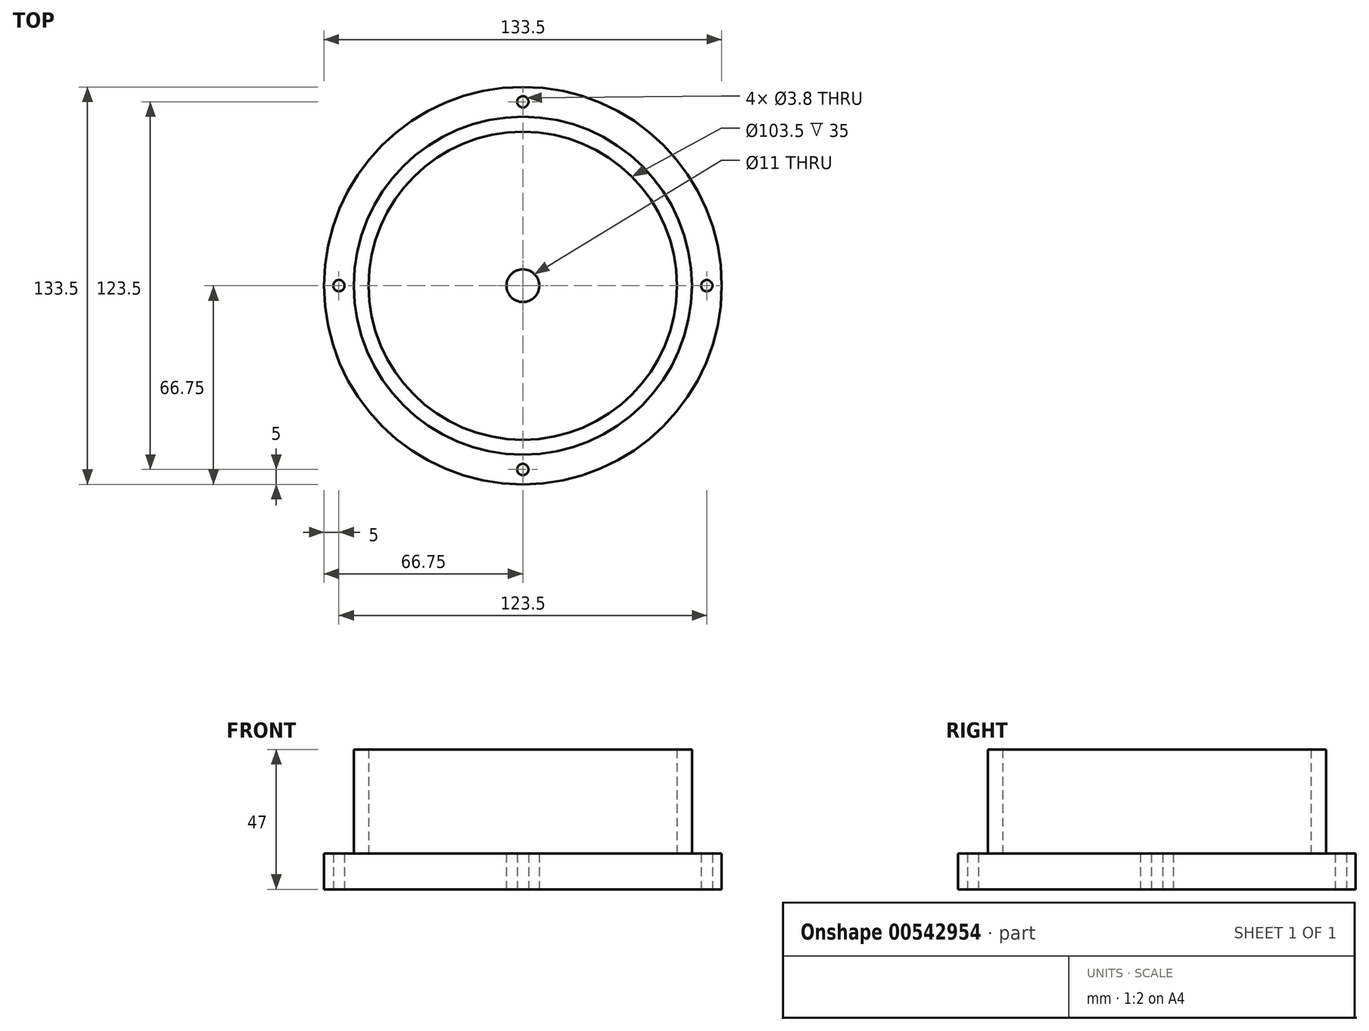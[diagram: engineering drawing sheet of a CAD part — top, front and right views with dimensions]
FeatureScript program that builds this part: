
annotation { "Feature Type Name" : "Feature", "Feature Type Description" : "" }
export const myFeature = defineFeature(function(context is Context, id is Id, definition is map)
    precondition{}
    {
        {
            var Q0;
            Q0=qCreatedBy(makeId("Top.planeOp"),FACE);
            var sketch = newSketch(context, id + "F0", { "sketchPlane" : qUnion([Q0])});
            skCircle(sketch, "E0", {"center": v(0, 0) * mm, "radius": 66.75 * mm});
            skSolve(sketch);
        }
        {
            var Q0;
            Q0 = qSketchRegion(id + "F0", true);
            extrude(context, id + "F1", {"entities" : qUnion([Q0]), "depth" : 12 * mm, "offsetDistance" : 25 * mm});
        }
        {
            var Q0;
            Q0=makeQuery(id+"F1.opExtrude","CAP_FACE",FACE,{"disambiguationData":[OSD([sQuery(id+"F0.wireOp",EDGE,"E0")])],"isStart":false});
            var sketch = newSketch(context, id + "F2", { "sketchPlane" : qUnion([Q0])});
            skCircle(sketch, "E1", {"center": v(0, 0) * mm, "radius": 56.75 * mm});
            skCircle(sketch, "E2", {"center": v(0, 0) * mm, "radius": 51.75 * mm});
            skSolve(sketch);
        }
        {
            var Q0;
            Q0=makeQuery(id+"F2.imprint","IMPRINT",FACE,{"disambiguationData":[TD([[makeQuery(id+"F2.imprint","IMPRINT",EDGE,{"derivedFrom":sQuery(id+"F2.wireOp",EDGE,"E1")}),1.0]])]});
            extrude(context, id + "F3", {"entities" : qUnion([Q0]), "operationType" : NewBodyOperationType.ADD, "depth" : 35 * mm, "offsetDistance" : 25 * mm});
        }
        {
            var Q0;
            Q0=qCreatedBy(makeId("Top.planeOp"),FACE);
            var sketch = newSketch(context, id + "F4", { "sketchPlane" : qUnion([Q0])});
            skCircle(sketch, "E3", {"center": v(0, 0) * mm, "radius": 61.75 * mm, "construction": true});
            skSolve(sketch);
        }
        {
            var Q0;
            Q0=qCreatedBy(makeId("Top.planeOp"),FACE);
            var sketch = newSketch(context, id + "F5", { "sketchPlane" : qUnion([Q0])});
            skCircle(sketch, "E4.0", {"center": v(0, 0) * mm, "radius": 61.75 * mm});
            skCircle(sketch, "E5", {"center": v(-61.75, 0) * mm, "radius": 1.9 * mm});
            skCircle(sketch, "E6", {"center": v(0, -61.75) * mm, "radius": 1.9 * mm});
            skCircle(sketch, "E7", {"center": v(61.75, 0) * mm, "radius": 1.9 * mm});
            skCircle(sketch, "E8", {"center": v(0, 61.75) * mm, "radius": 1.9 * mm});
            skSolve(sketch);
        }
        {
            var Q0;
            {var subQ0=sQuery(id+"F5.wireOp",EDGE,"E8");var subQ1=sQuery(id+"F5.wireOp",EDGE,"E4.0");var subQ2=makeQuery(id+"F5.imprint","INTERSECT",VERTEX,{"disambiguationData":[OD(0.0)],"derivedFrom":[subQ1,subQ0]});Q0=makeQuery(id+"F5.imprint","IMPRINT",FACE,{"disambiguationData":[TD([[makeQuery(id+"F5.imprint","IMPRINT",EDGE,{"disambiguationData":[TD([[subQ2,-1.0]])],"derivedFrom":subQ1}),1.0]])]});}
            var Q1;
            {var subQ0=sQuery(id+"F5.wireOp",EDGE,"E8");var subQ1=sQuery(id+"F5.wireOp",EDGE,"E4.0");var subQ2=makeQuery(id+"F5.imprint","INTERSECT",VERTEX,{"disambiguationData":[OD(0.0)],"derivedFrom":[subQ1,subQ0]});Q1=makeQuery(id+"F5.imprint","IMPRINT",FACE,{"disambiguationData":[TD([[makeQuery(id+"F5.imprint","IMPRINT",EDGE,{"disambiguationData":[TD([[subQ2,-1.0]])],"derivedFrom":subQ1}),-1.0]])]});}
            var Q2;
            {var subQ0=sQuery(id+"F5.wireOp",EDGE,"E7");var subQ1=sQuery(id+"F5.wireOp",EDGE,"E4.0");var subQ2=makeQuery(id+"F5.imprint","INTERSECT",VERTEX,{"disambiguationData":[OD(0.0)],"derivedFrom":[subQ1,subQ0]});Q2=makeQuery(id+"F5.imprint","IMPRINT",FACE,{"disambiguationData":[TD([[makeQuery(id+"F5.imprint","IMPRINT",EDGE,{"disambiguationData":[TD([[subQ2,1.0]])],"derivedFrom":subQ1}),-1.0]])]});}
            var Q3;
            {var subQ0=sQuery(id+"F5.wireOp",EDGE,"E7");var subQ1=sQuery(id+"F5.wireOp",EDGE,"E4.0");var subQ2=makeQuery(id+"F5.imprint","INTERSECT",VERTEX,{"disambiguationData":[OD(0.0)],"derivedFrom":[subQ1,subQ0]});Q3=makeQuery(id+"F5.imprint","IMPRINT",FACE,{"disambiguationData":[TD([[makeQuery(id+"F5.imprint","IMPRINT",EDGE,{"disambiguationData":[TD([[subQ2,1.0]])],"derivedFrom":subQ1}),1.0]])]});}
            var Q4;
            {var subQ0=sQuery(id+"F5.wireOp",EDGE,"E6");var subQ1=sQuery(id+"F5.wireOp",EDGE,"E4.0");var subQ2=makeQuery(id+"F5.imprint","INTERSECT",VERTEX,{"disambiguationData":[OD(0.0)],"derivedFrom":[subQ1,subQ0]});Q4=makeQuery(id+"F5.imprint","IMPRINT",FACE,{"disambiguationData":[TD([[makeQuery(id+"F5.imprint","IMPRINT",EDGE,{"disambiguationData":[TD([[subQ2,-1.0]])],"derivedFrom":subQ1}),-1.0]])]});}
            var Q5;
            {var subQ0=sQuery(id+"F5.wireOp",EDGE,"E6");var subQ1=sQuery(id+"F5.wireOp",EDGE,"E4.0");var subQ2=makeQuery(id+"F5.imprint","INTERSECT",VERTEX,{"disambiguationData":[OD(0.0)],"derivedFrom":[subQ1,subQ0]});Q5=makeQuery(id+"F5.imprint","IMPRINT",FACE,{"disambiguationData":[TD([[makeQuery(id+"F5.imprint","IMPRINT",EDGE,{"disambiguationData":[TD([[subQ2,-1.0]])],"derivedFrom":subQ1}),1.0]])]});}
            var Q6;
            {var subQ0=sQuery(id+"F5.wireOp",EDGE,"E5");var subQ1=sQuery(id+"F5.wireOp",EDGE,"E4.0");var subQ2=makeQuery(id+"F5.imprint","INTERSECT",VERTEX,{"disambiguationData":[OD(0.0)],"derivedFrom":[subQ1,subQ0]});Q6=makeQuery(id+"F5.imprint","IMPRINT",FACE,{"disambiguationData":[TD([[makeQuery(id+"F5.imprint","IMPRINT",EDGE,{"disambiguationData":[TD([[subQ2,-1.0]])],"derivedFrom":subQ1}),1.0]])]});}
            var Q7;
            {var subQ0=sQuery(id+"F5.wireOp",EDGE,"E5");var subQ1=sQuery(id+"F5.wireOp",EDGE,"E4.0");var subQ2=makeQuery(id+"F5.imprint","INTERSECT",VERTEX,{"disambiguationData":[OD(0.0)],"derivedFrom":[subQ1,subQ0]});Q7=makeQuery(id+"F5.imprint","IMPRINT",FACE,{"disambiguationData":[TD([[makeQuery(id+"F5.imprint","IMPRINT",EDGE,{"disambiguationData":[TD([[subQ2,-1.0]])],"derivedFrom":subQ1}),-1.0]])]});}
            extrude(context, id + "F6", {"entities" : qUnion([Q0, Q1, Q2, Q3, Q4, Q5, Q6, Q7]), "operationType" : NewBodyOperationType.REMOVE, "depth" : 12 * mm, "offsetDistance" : 25 * mm});
        }
        {
            var Q0;
            Q0=qCreatedBy(makeId("Top.planeOp"),FACE);
            var sketch = newSketch(context, id + "F7", { "sketchPlane" : qUnion([Q0])});
            skCircle(sketch, "E9", {"center": v(0, 0) * mm, "radius": 5.5 * mm});
            skSolve(sketch);
        }
        {
            var Q0;
            Q0=makeQuery(id+"F7.imprint","IMPRINT",FACE,{"disambiguationData":[TD([[makeQuery(id+"F7.imprint","IMPRINT",EDGE,{"derivedFrom":sQuery(id+"F7.wireOp",EDGE,"E9")}),1.0]])]});
            extrude(context, id + "F8", {"entities" : qUnion([Q0]), "operationType" : NewBodyOperationType.REMOVE, "depth" : 12 * mm, "offsetDistance" : 25 * mm});
        }
    });
